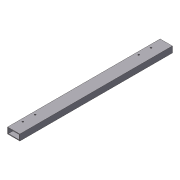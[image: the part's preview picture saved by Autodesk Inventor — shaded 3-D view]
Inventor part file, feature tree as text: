
AUTODESK INVENTOR PART (.ipt)
format: ipt  version: 2012 (Build 160160000, 160)  size: 94,208 bytes
history: native  units: in
note: dims shown in document units (in); Inventor stores cm internally (conversion verified against a paired STEP export)
features: extrude x2, sketch x2, shell x1
ambient origin geometry x8: Origin, YZ Plane, XZ Plane, XY Plane, X Axis, Y Axis, Z Axis, Center Point
bodies: Solid1 (feature_tree)
feature tree (5):
  extrude  "Extrusion1"  Depth=2.0in
  shell  "Shell1"  Thickness=25.0in
  extrude  "Extrusion2"  Depth=2.0in
  sketch  "Sketch1"  dims[d0=1.0in d1=2.0in d2=25.0in d3=0.0in]
  sketch  "Sketch2"  dims[d4=0.5in d5=2.0in d6=2.0in d7=0.25in d8=0.25in d9=0.25in d10=0.25in d11=25.0in d12=0.0in d13=0.125in]
